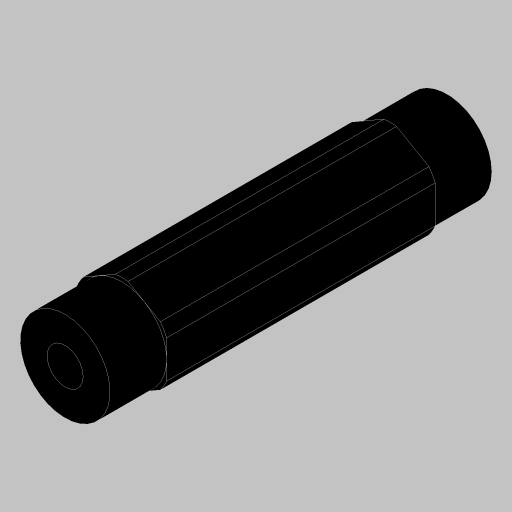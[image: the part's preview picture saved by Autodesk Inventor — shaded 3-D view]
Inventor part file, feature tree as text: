
AUTODESK INVENTOR PART (.ipt)
format: ipt  version: 2023.5 (Build 275446000, 446)  size: 167,424 bytes
history: native  units: in
note: dims shown in document units (in); Inventor stores cm internally (conversion verified against a paired STEP export)
features: extrude x3, projected_geometry x3, hole x1, mirror x1, sketch x1
ambient origin geometry x8: Origin, YZ Plane, XZ Plane, XY Plane, X Axis, Y Axis, Z Axis, Center Point
bodies: Solid1 (feature_tree)
feature tree (9):
  extrude  "Extrusion1"  Depth=0.315in
  hole  "Hole1"  [1 undecoded]
  extrude  "Extrusion3"  Depth=0.5in
  extrude  "Extrusion4"  Depth=0.315in TaperAngle=0.0deg
  mirror  "Mirror2"
  sketch  "Sketch5"  dims[d2=0.0in d9=0.625in d10=0.385in d11=0.25in d12=0.5635in d13=1.0in d14=0.8108in d16=0.7in d17=0.0in d18=0.0in d19=0.5in d20=0.315in d21=0.0in]
  projected_geometry  "Project Cut Edges1"
  projected_geometry  "Project Cut Edges2"
  projected_geometry  "Project Cut Edges3"
note: 1 required parameter value undecoded (feature->parameter linkage not recoverable at this tier; creation-order binding heuristic only, values carry confidence <= 0.55)
